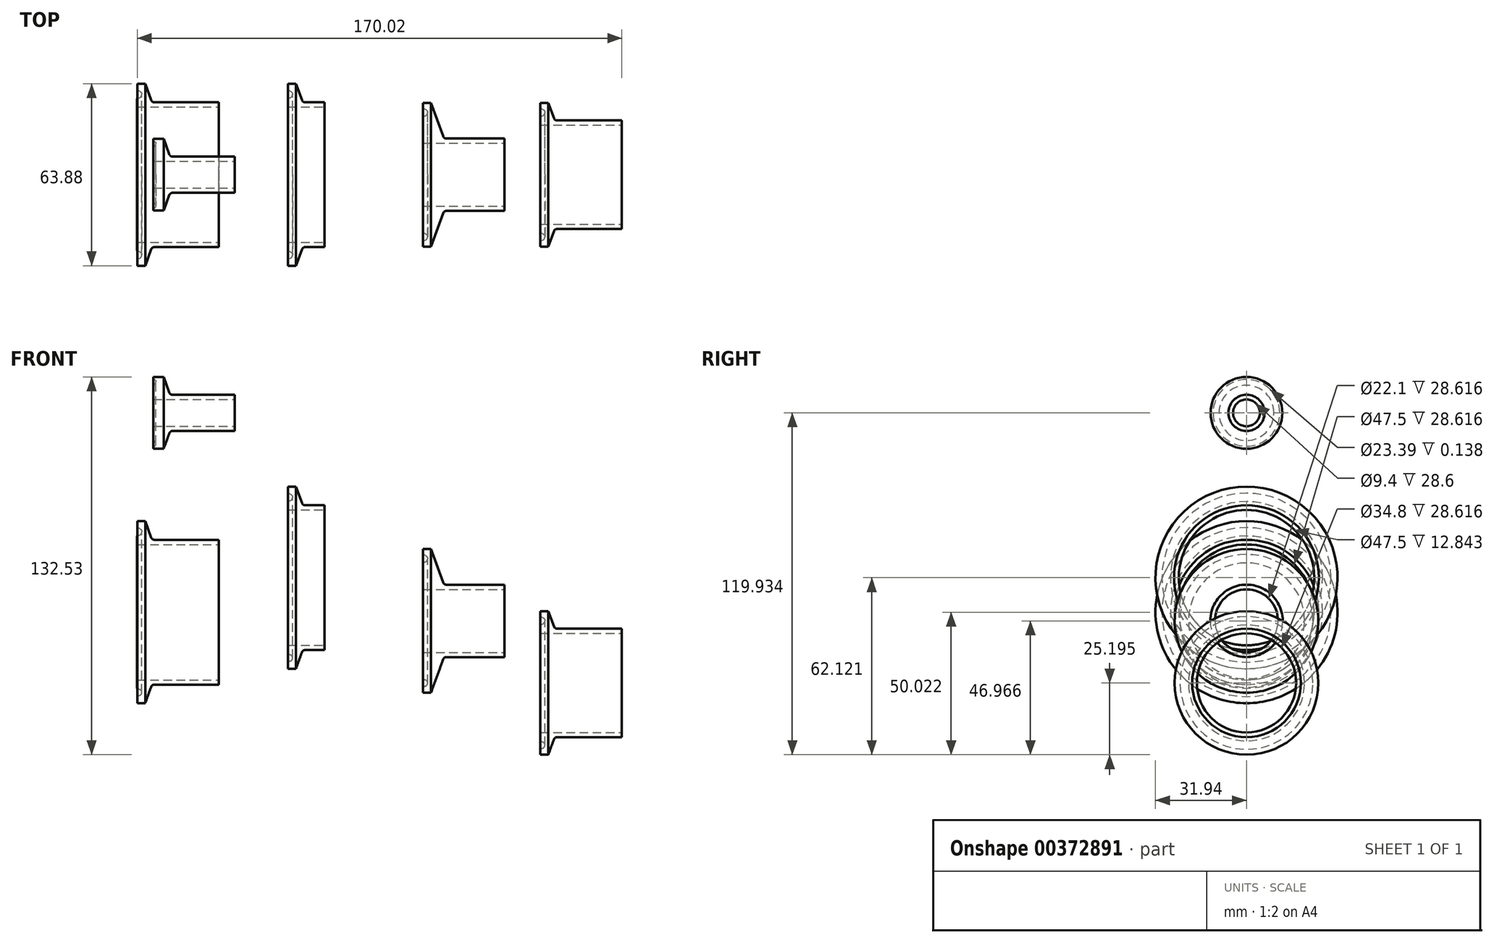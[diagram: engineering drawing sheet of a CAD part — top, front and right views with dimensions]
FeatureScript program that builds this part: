
annotation { "Feature Type Name" : "Feature", "Feature Type Description" : "" }
export const myFeature = defineFeature(function(context is Context, id is Id, definition is map)
    precondition{}
    {
        {
            var Q0;
            Q0=qCreatedBy(makeId("Front.planeOp"),FACE);
            var sketch = newSketch(context, id + "F0", { "sketchPlane" : qUnion([Q0])});
            skLineSegment(sketch, "E0", {"start": v(-12.83, 14.73) * mm, "end": v(-10.02, 14.73) * mm});
            skLineSegment(sketch, "E1", {"start": v(-10.02, 14.73) * mm, "end": v(-7.64, 8.2) * mm, "construction": true});
            skLineSegment(sketch, "E2", {"start": v(-7.64, 8.2) * mm, "end": v(0, 8.2) * mm, "construction": true});
            skLineSegment(sketch, "E3", {"start": v(0, 8.2) * mm, "end": v(0, -17.2) * mm});
            skLineSegment(sketch, "E4", {"start": v(0, -17.2) * mm, "end": v(-12.78, -17.2) * mm, "construction": true});
            skLineSegment(sketch, "E5", {"start": v(-11.21, 14.73) * mm, "end": v(-11.21, -17.2) * mm, "construction": true});
            skLineSegment(sketch, "E6", {"start": v(0, 6.54) * mm, "end": v(-12.84, 6.54) * mm});
            skArc(sketch, "E7", {"start": v(-7.91, 8.94) * mm, "mid": v(-7.5, 8.4) * mm, "end": v(-6.84, 8.2) * mm});
            skLineSegment(sketch, "E8", {"start": v(-12.83, 12.44) * mm, "end": v(-11.21, 11.75) * mm, "construction": true});
            skLineSegment(sketch, "E9", {"start": v(-12.84, 9.48) * mm, "end": v(-11.21, 10.17) * mm, "construction": true});
            skArc(sketch, "E10", {"start": v(-11.21, 10.96) * mm, "mid": v(-11.4, 11.62) * mm, "end": v(-11.94, 12.06) * mm});
            skArc(sketch, "E11", {"start": v(-11.94, 9.86) * mm, "mid": v(-11.4, 10.3) * mm, "end": v(-11.21, 10.96) * mm});
            skLineSegment(sketch, "E12", {"start": v(-12.83, 14.73) * mm, "end": v(-12.83, 12.44) * mm});
            skLineSegment(sketch, "E13", {"start": v(-12.84, 9.48) * mm, "end": v(-12.84, 6.54) * mm});
            skLineSegment(sketch, "E14", {"start": v(-7.91, 8.94) * mm, "end": v(-10.02, 14.73) * mm});
            skLineSegment(sketch, "E15", {"start": v(-6.84, 8.2) * mm, "end": v(0, 8.2) * mm});
            skLineSegment(sketch, "E16", {"start": v(-12.83, 12.44) * mm, "end": v(-11.94, 12.06) * mm});
            skLineSegment(sketch, "E17", {"start": v(-12.84, 9.48) * mm, "end": v(-11.94, 9.86) * mm});
            skLineSegment(sketch, "E18", {"start": v(-11.21, 10.96) * mm, "end": v(-11.21, 10.96) * mm});
            skLineSegment(sketch, "E19", {"start": v(-11.21, 10.96) * mm, "end": v(-16.43, 10.96) * mm, "construction": true});
            skSolve(sketch);
        }
        {
            var Q0;
            Q0 = qSketchRegion(id + "F0", true);
            var Q1;
            Q1=sQuery(id+"F0.wireOp",EDGE,"E4");
            revolve(context, id + "F1", {"entities" : qUnion([Q0]), "axis" : qUnion([Q1]), "revolveType" : RevolveType.FULL});
        }
        {
            var Q0;
            Q0=qCreatedBy(makeId("Front.planeOp"),FACE);
            var sketch = newSketch(context, id + "F2", { "sketchPlane" : qUnion([Q0])});
            skLineSegment(sketch, "E20", {"start": v(-65.7, 2.63) * mm, "end": v(-62.89, 2.63) * mm});
            skLineSegment(sketch, "E21", {"start": v(-62.89, 2.63) * mm, "end": v(-60.5, -3.9) * mm, "construction": true});
            skLineSegment(sketch, "E22", {"start": v(-60.5, -3.9) * mm, "end": v(-37.1, -3.9) * mm, "construction": true});
            skLineSegment(sketch, "E23", {"start": v(-37.1, -3.9) * mm, "end": v(-37.1, -29.3) * mm});
            skLineSegment(sketch, "E24", {"start": v(-37.1, -29.3) * mm, "end": v(-64.08, -29.3) * mm, "construction": true});
            skLineSegment(sketch, "E25", {"start": v(-64.08, 2.63) * mm, "end": v(-64.08, -29.3) * mm, "construction": true});
            skLineSegment(sketch, "E26", {"start": v(-37.1, -5.56) * mm, "end": v(-65.71, -5.56) * mm});
            skArc(sketch, "E27", {"start": v(-60.78, -3.16) * mm, "mid": v(-60.36, -3.7) * mm, "end": v(-59.7, -3.9) * mm});
            skLineSegment(sketch, "E28", {"start": v(-65.7, 0.34) * mm, "end": v(-64.08, -0.35) * mm, "construction": true});
            skLineSegment(sketch, "E29", {"start": v(-65.71, -2.62) * mm, "end": v(-64.08, -1.93) * mm, "construction": true});
            skArc(sketch, "E30", {"start": v(-64.08, -1.14) * mm, "mid": v(-64.28, -0.48) * mm, "end": v(-64.8, -0.04) * mm});
            skArc(sketch, "E31", {"start": v(-64.8, -2.24) * mm, "mid": v(-64.28, -1.8) * mm, "end": v(-64.08, -1.14) * mm});
            skLineSegment(sketch, "E32", {"start": v(-65.7, 2.63) * mm, "end": v(-65.7, 0.34) * mm});
            skLineSegment(sketch, "E33", {"start": v(-65.71, -2.62) * mm, "end": v(-65.71, -5.56) * mm});
            skLineSegment(sketch, "E34", {"start": v(-60.78, -3.16) * mm, "end": v(-62.89, 2.63) * mm});
            skLineSegment(sketch, "E35", {"start": v(-59.7, -3.9) * mm, "end": v(-37.1, -3.9) * mm});
            skLineSegment(sketch, "E36", {"start": v(-65.7, 0.34) * mm, "end": v(-64.8, -0.04) * mm});
            skLineSegment(sketch, "E37", {"start": v(-65.71, -2.62) * mm, "end": v(-64.8, -2.24) * mm});
            skLineSegment(sketch, "E38", {"start": v(-64.08, -1.14) * mm, "end": v(-64.08, -1.14) * mm});
            skLineSegment(sketch, "E39", {"start": v(-64.08, -1.14) * mm, "end": v(-65.71, -1.14) * mm, "construction": true});
            skSolve(sketch);
        }
        {
            var Q0;
            Q0 = qSketchRegion(id + "F2", true);
            var Q1;
            Q1=sQuery(id+"F2.wireOp",EDGE,"E24");
            revolve(context, id + "F3", {"entities" : qUnion([Q0]), "axis" : qUnion([Q1]), "revolveType" : RevolveType.FULL});
        }
        {
            var Q0;
            Q0=qCreatedBy(makeId("Front.planeOp"),FACE);
            var sketch = newSketch(context, id + "F4", { "sketchPlane" : qUnion([Q0])});
            skLineSegment(sketch, "E40", {"start": v(34.56, -7.17) * mm, "end": v(37.36, -7.17) * mm});
            skLineSegment(sketch, "E41", {"start": v(37.36, -7.17) * mm, "end": v(41.91, -19.66) * mm, "construction": true});
            skLineSegment(sketch, "E42", {"start": v(41.91, -19.66) * mm, "end": v(63.16, -19.66) * mm, "construction": true});
            skLineSegment(sketch, "E43", {"start": v(63.16, -19.66) * mm, "end": v(63.16, -32.36) * mm});
            skLineSegment(sketch, "E44", {"start": v(63.16, -32.36) * mm, "end": v(36.17, -32.36) * mm, "construction": true});
            skLineSegment(sketch, "E45", {"start": v(36.17, -7.17) * mm, "end": v(36.17, -32.36) * mm, "construction": true});
            skLineSegment(sketch, "E46", {"start": v(63.16, -21.31) * mm, "end": v(34.54, -21.31) * mm});
            skArc(sketch, "E47", {"start": v(41.64, -18.91) * mm, "mid": v(42.06, -19.46) * mm, "end": v(42.71, -19.66) * mm});
            skLineSegment(sketch, "E48", {"start": v(34.56, -9.07) * mm, "end": v(36.17, -9.75) * mm, "construction": true});
            skLineSegment(sketch, "E49", {"start": v(34.54, -12.03) * mm, "end": v(36.17, -11.34) * mm, "construction": true});
            skArc(sketch, "E50", {"start": v(36.17, -10.55) * mm, "mid": v(35.97, -9.89) * mm, "end": v(35.45, -9.45) * mm});
            skArc(sketch, "E51", {"start": v(35.45, -11.64) * mm, "mid": v(35.97, -11.2) * mm, "end": v(36.17, -10.55) * mm});
            skLineSegment(sketch, "E52", {"start": v(34.56, -7.17) * mm, "end": v(34.56, -9.07) * mm});
            skLineSegment(sketch, "E53", {"start": v(34.54, -12.03) * mm, "end": v(34.54, -21.31) * mm});
            skLineSegment(sketch, "E54", {"start": v(41.64, -18.91) * mm, "end": v(37.36, -7.17) * mm});
            skLineSegment(sketch, "E55", {"start": v(42.71, -19.66) * mm, "end": v(63.16, -19.66) * mm});
            skLineSegment(sketch, "E56", {"start": v(34.56, -9.07) * mm, "end": v(35.45, -9.45) * mm});
            skLineSegment(sketch, "E57", {"start": v(34.54, -12.03) * mm, "end": v(35.45, -11.64) * mm});
            skLineSegment(sketch, "E58", {"start": v(36.17, -10.55) * mm, "end": v(36.17, -10.55) * mm});
            skLineSegment(sketch, "E59", {"start": v(36.17, -10.55) * mm, "end": v(34.54, -10.55) * mm, "construction": true});
            skSolve(sketch);
        }
        {
            var Q0;
            Q0=makeQuery(id+"F4.imprint","IMPRINT",FACE,{"disambiguationData":[TD([[makeQuery(id+"F4.imprint","IMPRINT",EDGE,{"derivedFrom":sQuery(id+"F4.wireOp",EDGE,"E40")}),-1.0]])]});
            var Q1;
            Q1=sQuery(id+"F4.wireOp",EDGE,"E44");
            revolve(context, id + "F5", {"entities" : qUnion([Q0]), "axis" : qUnion([Q1]), "revolveType" : RevolveType.FULL});
        }
        {
            var Q0;
            Q0=qCreatedBy(makeId("Front.planeOp"),FACE);
            var sketch = newSketch(context, id + "F6", { "sketchPlane" : qUnion([Q0])});
            skLineSegment(sketch, "E60", {"start": v(75.7, -28.94) * mm, "end": v(78.52, -28.94) * mm});
            skLineSegment(sketch, "E61", {"start": v(78.52, -28.94) * mm, "end": v(80.75, -35.08) * mm, "construction": true});
            skLineSegment(sketch, "E62", {"start": v(80.75, -35.08) * mm, "end": v(104.3, -35.08) * mm, "construction": true});
            skLineSegment(sketch, "E63", {"start": v(104.3, -35.08) * mm, "end": v(104.3, -54.13) * mm});
            skLineSegment(sketch, "E64", {"start": v(104.3, -54.13) * mm, "end": v(77.33, -54.13) * mm, "construction": true});
            skLineSegment(sketch, "E65", {"start": v(77.33, -28.94) * mm, "end": v(77.33, -54.13) * mm, "construction": true});
            skLineSegment(sketch, "E66", {"start": v(104.3, -36.74) * mm, "end": v(75.7, -36.74) * mm});
            skArc(sketch, "E67", {"start": v(80.48, -34.33) * mm, "mid": v(80.9, -34.88) * mm, "end": v(81.55, -35.08) * mm});
            skLineSegment(sketch, "E68", {"start": v(75.7, -30.84) * mm, "end": v(77.33, -31.53) * mm, "construction": true});
            skLineSegment(sketch, "E69", {"start": v(75.7, -33.8) * mm, "end": v(77.33, -33.1) * mm, "construction": true});
            skArc(sketch, "E70", {"start": v(77.33, -32.32) * mm, "mid": v(77.13, -31.66) * mm, "end": v(76.6, -31.22) * mm});
            skArc(sketch, "E71", {"start": v(76.6, -33.41) * mm, "mid": v(77.13, -32.97) * mm, "end": v(77.33, -32.32) * mm});
            skLineSegment(sketch, "E72", {"start": v(75.7, -28.94) * mm, "end": v(75.7, -30.84) * mm});
            skLineSegment(sketch, "E73", {"start": v(75.7, -33.8) * mm, "end": v(75.7, -36.74) * mm});
            skLineSegment(sketch, "E74", {"start": v(80.48, -34.33) * mm, "end": v(78.52, -28.94) * mm});
            skLineSegment(sketch, "E75", {"start": v(81.55, -35.08) * mm, "end": v(104.3, -35.08) * mm});
            skLineSegment(sketch, "E76", {"start": v(75.7, -30.84) * mm, "end": v(76.6, -31.22) * mm});
            skLineSegment(sketch, "E77", {"start": v(75.7, -33.8) * mm, "end": v(76.6, -33.41) * mm});
            skLineSegment(sketch, "E78", {"start": v(77.33, -32.32) * mm, "end": v(77.33, -32.32) * mm});
            skLineSegment(sketch, "E79", {"start": v(77.33, -32.32) * mm, "end": v(75.7, -32.32) * mm, "construction": true});
            skSolve(sketch);
        }
        {
            var Q0;
            Q0 = qSketchRegion(id + "F6", true);
            var Q1;
            Q1=sQuery(id+"F6.wireOp",EDGE,"E64");
            revolve(context, id + "F7", {"entities" : qUnion([Q0]), "axis" : qUnion([Q1]), "revolveType" : RevolveType.FULL});
        }
        {
            var Q0;
            Q0=qCreatedBy(makeId("Front.planeOp"),FACE);
            var sketch = newSketch(context, id + "F8", { "sketchPlane" : qUnion([Q0])});
            skLineSegment(sketch, "E80", {"start": v(-60.03, 53.2) * mm, "end": v(-56.4, 53.2) * mm});
            skLineSegment(sketch, "E81", {"start": v(-56.4, 53.2) * mm, "end": v(-54.13, 46.95) * mm, "construction": true});
            skLineSegment(sketch, "E82", {"start": v(-54.13, 46.95) * mm, "end": v(-31.43, 46.95) * mm, "construction": true});
            skLineSegment(sketch, "E83", {"start": v(-31.43, 46.95) * mm, "end": v(-31.43, 40.6) * mm});
            skLineSegment(sketch, "E84", {"start": v(-31.43, 40.6) * mm, "end": v(-59.1, 40.6) * mm, "construction": true});
            skLineSegment(sketch, "E85", {"start": v(-59.1, 53.2) * mm, "end": v(-59.1, 40.6) * mm, "construction": true});
            skLineSegment(sketch, "E86", {"start": v(-31.43, 45.3) * mm, "end": v(-60.03, 45.3) * mm});
            skArc(sketch, "E87", {"start": v(-54.4, 47.7) * mm, "mid": v(-53.98, 47.16) * mm, "end": v(-53.33, 46.95) * mm});
            skLineSegment(sketch, "E88", {"start": v(-60.03, 52.3) * mm, "end": v(-59.1, 52.3) * mm, "construction": true});
            skLineSegment(sketch, "E89", {"start": v(-60.03, 50.26) * mm, "end": v(-59.1, 51.19) * mm, "construction": true});
            skArc(sketch, "E90", {"start": v(-59.1, 51.51) * mm, "mid": v(-59.34, 52.07) * mm, "end": v(-59.9, 52.3) * mm});
            skArc(sketch, "E91", {"start": v(-59.34, 50.96) * mm, "mid": v(-59.17, 51.21) * mm, "end": v(-59.1, 51.51) * mm});
            skLineSegment(sketch, "E92", {"start": v(-60.03, 53.2) * mm, "end": v(-60.03, 52.3) * mm});
            skLineSegment(sketch, "E93", {"start": v(-60.03, 50.26) * mm, "end": v(-60.03, 45.3) * mm});
            skLineSegment(sketch, "E94", {"start": v(-54.4, 47.7) * mm, "end": v(-56.4, 53.2) * mm});
            skLineSegment(sketch, "E95", {"start": v(-53.33, 46.95) * mm, "end": v(-31.43, 46.95) * mm});
            skLineSegment(sketch, "E96", {"start": v(-60.03, 52.3) * mm, "end": v(-59.9, 52.3) * mm});
            skLineSegment(sketch, "E97", {"start": v(-60.03, 50.26) * mm, "end": v(-59.34, 50.96) * mm});
            skLineSegment(sketch, "E98", {"start": v(-59.1, 51.51) * mm, "end": v(-59.1, 51.51) * mm});
            skLineSegment(sketch, "E99", {"start": v(-59.1, 51.51) * mm, "end": v(-60.03, 51.51) * mm, "construction": true});
            skSolve(sketch);
        }
        {
            var Q0;
            Q0=makeQuery(id+"F8.imprint","IMPRINT",FACE,{"disambiguationData":[TD([[makeQuery(id+"F8.imprint","IMPRINT",EDGE,{"derivedFrom":sQuery(id+"F8.wireOp",EDGE,"E80")}),-1.0]])]});
            var Q1;
            Q1=sQuery(id+"F8.wireOp",EDGE,"E84");
            revolve(context, id + "F9", {"entities" : qUnion([Q0]), "axis" : qUnion([Q1]), "revolveType" : RevolveType.FULL});
        }
    });
